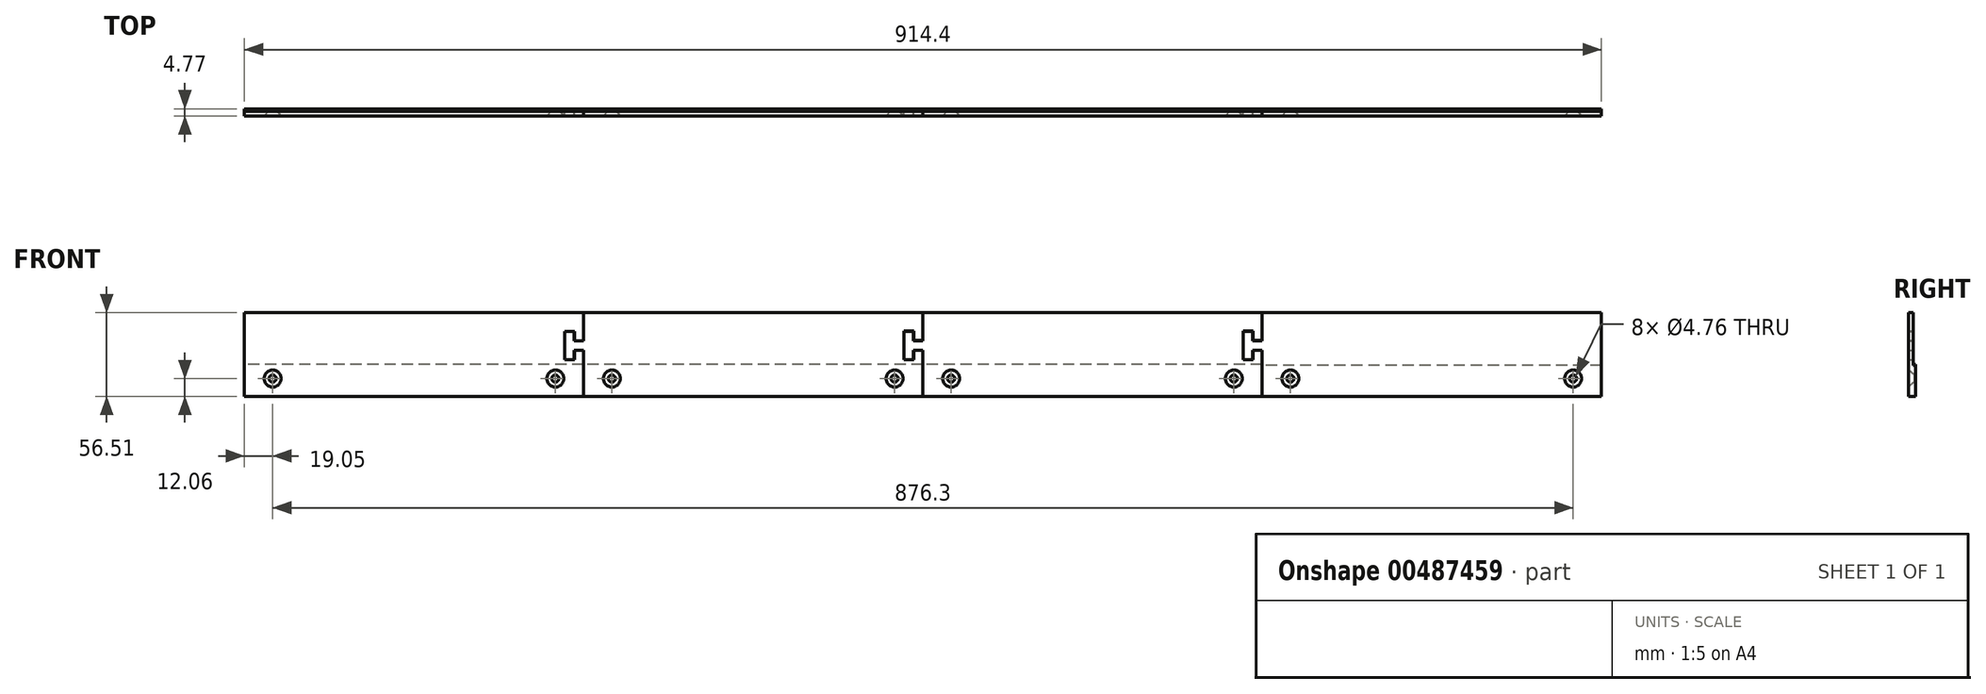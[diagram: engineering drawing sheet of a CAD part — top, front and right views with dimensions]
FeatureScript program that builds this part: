
annotation { "Feature Type Name" : "Feature", "Feature Type Description" : "" }
export const myFeature = defineFeature(function(context is Context, id is Id, definition is map)
    precondition{}
    {
        {
            var Q0;
            Q0=qCreatedBy(makeId("Front.planeOp"),FACE);
            var sketch = newSketch(context, id + "F0", { "sketchPlane" : qUnion([Q0])});
            skLineSegment(sketch, "E0.bottom", {"start": v(0, 0) * mm, "end": v(228.45, 0) * mm});
            skLineSegment(sketch, "E0.top", {"start": v(0, -63.5) * mm, "end": v(228.45, -63.5) * mm});
            skLineSegment(sketch, "E0.right", {"start": v(457.2, 0) * mm, "end": v(457.2, -63.5) * mm});
            skCircle(sketch, "E1", {"center": v(438.15, -44.45) * mm, "radius": 2.38 * mm});
            skLineSegment(sketch, "E2.MirrorCS", {"start": v(-0.15, 0) * mm, "end": v(-228.6, 0) * mm});
            skLineSegment(sketch, "E3.MirrorCS", {"start": v(-0.15, -63.5) * mm, "end": v(-228.6, -63.5) * mm});
            skLineSegment(sketch, "E4.MirrorCS", {"start": v(-457.2, 0) * mm, "end": v(-457.2, -63.5) * mm});
            skCircle(sketch, "E5.MirrorC", {"center": v(-438.15, -44.45) * mm, "radius": 2.38 * mm});
            skLineSegment(sketch, "E6", {"start": v(-228.6, 0) * mm, "end": v(-228.6, -19.05) * mm});
            skLineSegment(sketch, "E7", {"start": v(0, 0) * mm, "end": v(0, -18.9) * mm});
            skLineSegment(sketch, "E8", {"start": v(228.6, 0) * mm, "end": v(228.6, -18.9) * mm});
            skLineSegment(sketch, "E9", {"start": v(-228.6, -19.05) * mm, "end": v(-234.95, -19.05) * mm});
            skLineSegment(sketch, "E10", {"start": v(-234.95, -19.05) * mm, "end": v(-234.95, -12.7) * mm});
            skLineSegment(sketch, "E11", {"start": v(-234.95, -12.7) * mm, "end": v(-241.3, -12.7) * mm});
            skLineSegment(sketch, "E12", {"start": v(-241.3, -12.7) * mm, "end": v(-241.3, -31.75) * mm});
            skLineSegment(sketch, "E13", {"start": v(-241.3, -31.75) * mm, "end": v(-234.95, -31.75) * mm});
            skLineSegment(sketch, "E14", {"start": v(-234.95, -31.75) * mm, "end": v(-234.95, -25.4) * mm});
            skLineSegment(sketch, "E15", {"start": v(-234.95, -25.4) * mm, "end": v(-228.6, -25.4) * mm});
            skLineSegment(sketch, "E16", {"start": v(-228.75, 0) * mm, "end": v(-228.75, -18.9) * mm});
            skLineSegment(sketch, "E17", {"start": v(-228.75, -18.9) * mm, "end": v(-234.8, -18.9) * mm});
            skLineSegment(sketch, "E18", {"start": v(-234.8, -18.9) * mm, "end": v(-234.8, -12.55) * mm});
            skLineSegment(sketch, "E19", {"start": v(-234.8, -12.55) * mm, "end": v(-241.45, -12.55) * mm});
            skLineSegment(sketch, "E20", {"start": v(-241.45, -12.55) * mm, "end": v(-241.45, -31.9) * mm});
            skLineSegment(sketch, "E21.MirrorCS", {"start": v(-228.75, -63.5) * mm, "end": v(-228.75, -25.55) * mm});
            skLineSegment(sketch, "E22.MirrorCS", {"start": v(-228.75, -25.55) * mm, "end": v(-234.8, -25.55) * mm});
            skLineSegment(sketch, "E23.MirrorCS", {"start": v(-234.8, -25.55) * mm, "end": v(-234.8, -31.9) * mm});
            skLineSegment(sketch, "E24.MirrorCS", {"start": v(-234.8, -31.9) * mm, "end": v(-241.45, -31.9) * mm});
            skLineSegment(sketch, "E25.trimOffspring", {"start": v(-228.75, 0) * mm, "end": v(-457.2, 0) * mm});
            skLineSegment(sketch, "E26.trimOffspring", {"start": v(-228.6, -25.4) * mm, "end": v(-228.6, -63.5) * mm});
            skCircle(sketch, "E27", {"center": v(-247.65, -44.45) * mm, "radius": 2.38 * mm});
            skCircle(sketch, "E28.MirrorC", {"center": v(-209.55, -44.45) * mm, "radius": 2.38 * mm});
            skCircle(sketch, "E29.MirrorC", {"center": v(-19.05, -44.45) * mm, "radius": 2.38 * mm});
            skLineSegment(sketch, "E30.trimOffspring", {"start": v(-228.75, -63.5) * mm, "end": v(-457.2, -63.5) * mm});
            skCircle(sketch, "E31.MirrorC", {"center": v(19.05, -44.45) * mm, "radius": 2.38 * mm});
            skCircle(sketch, "E32.MirrorC", {"center": v(209.55, -44.45) * mm, "radius": 2.38 * mm});
            skCircle(sketch, "E33.MirrorC", {"center": v(247.65, -44.45) * mm, "radius": 2.38 * mm});
            skLineSegment(sketch, "E34", {"start": v(0, -18.9) * mm, "end": v(-6.35, -18.9) * mm});
            skLineSegment(sketch, "E35", {"start": v(-6.35, -18.9) * mm, "end": v(-6.35, -12.55) * mm});
            skLineSegment(sketch, "E36", {"start": v(-6.35, -12.55) * mm, "end": v(-12.7, -12.55) * mm});
            skLineSegment(sketch, "E37", {"start": v(-12.7, -12.55) * mm, "end": v(-12.7, -31.6) * mm});
            skLineSegment(sketch, "E38", {"start": v(-12.7, -31.6) * mm, "end": v(-6.35, -31.6) * mm});
            skLineSegment(sketch, "E39", {"start": v(-6.35, -31.6) * mm, "end": v(-6.35, -25.25) * mm});
            skLineSegment(sketch, "E40", {"start": v(-6.35, -25.25) * mm, "end": v(0, -25.25) * mm});
            skLineSegment(sketch, "E41", {"start": v(-0.15, -18.75) * mm, "end": v(-6.2, -18.75) * mm});
            skLineSegment(sketch, "E42", {"start": v(-6.2, -18.75) * mm, "end": v(-6.2, -12.4) * mm});
            skLineSegment(sketch, "E43", {"start": v(-6.2, -12.4) * mm, "end": v(-12.85, -12.4) * mm});
            skLineSegment(sketch, "E44", {"start": v(-12.85, -12.4) * mm, "end": v(-12.85, -31.75) * mm});
            skLineSegment(sketch, "E45.MirrorCS", {"start": v(-0.15, -25.4) * mm, "end": v(-6.2, -25.4) * mm});
            skLineSegment(sketch, "E46.MirrorCS", {"start": v(-6.2, -25.4) * mm, "end": v(-6.2, -31.75) * mm});
            skLineSegment(sketch, "E47.MirrorCS", {"start": v(-6.2, -31.75) * mm, "end": v(-12.85, -31.75) * mm});
            skLineSegment(sketch, "E48", {"start": v(-0.15, -18.75) * mm, "end": v(-0.15, 0) * mm});
            skLineSegment(sketch, "E49", {"start": v(-0.15, -25.4) * mm, "end": v(-0.15, -63.5) * mm});
            skLineSegment(sketch, "E50.trimOffspring", {"start": v(0, -25.25) * mm, "end": v(0, -63.5) * mm});
            skLineSegment(sketch, "E51", {"start": v(228.6, -18.9) * mm, "end": v(222.25, -18.9) * mm});
            skLineSegment(sketch, "E52", {"start": v(222.25, -18.9) * mm, "end": v(222.25, -12.55) * mm});
            skLineSegment(sketch, "E53", {"start": v(222.25, -12.55) * mm, "end": v(215.9, -12.55) * mm});
            skLineSegment(sketch, "E54", {"start": v(215.9, -12.55) * mm, "end": v(215.9, -31.6) * mm});
            skLineSegment(sketch, "E55", {"start": v(215.9, -31.6) * mm, "end": v(222.25, -31.6) * mm});
            skLineSegment(sketch, "E56", {"start": v(222.25, -31.6) * mm, "end": v(222.25, -25.25) * mm});
            skLineSegment(sketch, "E57", {"start": v(222.25, -25.25) * mm, "end": v(228.6, -25.25) * mm});
            skLineSegment(sketch, "E58", {"start": v(228.45, -18.75) * mm, "end": v(222.4, -18.75) * mm});
            skLineSegment(sketch, "E59", {"start": v(222.4, -18.75) * mm, "end": v(222.4, -12.4) * mm});
            skLineSegment(sketch, "E60", {"start": v(222.4, -12.4) * mm, "end": v(215.75, -12.4) * mm});
            skLineSegment(sketch, "E61", {"start": v(215.75, -12.4) * mm, "end": v(215.75, -31.75) * mm});
            skLineSegment(sketch, "E62.MirrorCS", {"start": v(228.45, -25.4) * mm, "end": v(222.4, -25.4) * mm});
            skLineSegment(sketch, "E63.MirrorCS", {"start": v(222.4, -25.4) * mm, "end": v(222.4, -31.75) * mm});
            skLineSegment(sketch, "E64.MirrorCS", {"start": v(222.4, -31.75) * mm, "end": v(215.75, -31.75) * mm});
            skLineSegment(sketch, "E65", {"start": v(228.45, -18.75) * mm, "end": v(228.45, 0) * mm});
            skLineSegment(sketch, "E66", {"start": v(228.45, -25.4) * mm, "end": v(228.45, -63.5) * mm});
            skLineSegment(sketch, "E67.trimOffspring", {"start": v(228.6, -63.5) * mm, "end": v(457.2, -63.5) * mm});
            skLineSegment(sketch, "E68.trimOffspring", {"start": v(228.6, 0) * mm, "end": v(457.2, 0) * mm});
            skLineSegment(sketch, "E69.trimOffspring", {"start": v(228.6, -25.25) * mm, "end": v(228.6, -63.5) * mm});
            skSolve(sketch);
        }
        {
            var Q0;
            Q0 = qSketchRegion(id + "F0", true);
            extrude(context, id + "F1", {"entities" : qUnion([Q0]), "depth" : 3.17 * mm, "offsetDistance" : 25.4 * mm});
        }
        {
            var Q0;
            Q0=makeQuery(id+"F1.opExtrude","CAP_FACE",FACE,{"disambiguationData":[OSD([sQuery(id+"F0.wireOp",EDGE,"E0.right"),sQuery(id+"F0.wireOp",EDGE,"E1"),sQuery(id+"F0.wireOp",EDGE,"E8"),sQuery(id+"F0.wireOp",EDGE,"E33.MirrorC"),sQuery(id+"F0.wireOp",EDGE,"E51"),sQuery(id+"F0.wireOp",EDGE,"E52"),sQuery(id+"F0.wireOp",EDGE,"E53"),sQuery(id+"F0.wireOp",EDGE,"E54"),sQuery(id+"F0.wireOp",EDGE,"E55"),sQuery(id+"F0.wireOp",EDGE,"E56"),sQuery(id+"F0.wireOp",EDGE,"E57"),sQuery(id+"F0.wireOp",EDGE,"E67.trimOffspring"),sQuery(id+"F0.wireOp",EDGE,"E68.trimOffspring"),sQuery(id+"F0.wireOp",EDGE,"E69.trimOffspring")])],"isStart":true});
            var sketch = newSketch(context, id + "F2", { "sketchPlane" : qUnion([Q0])});
            skLineSegment(sketch, "E70.bottom", {"start": v(-457.2, -35.72) * mm, "end": v(-228.6, -35.72) * mm});
            skLineSegment(sketch, "E70.top", {"start": v(-457.2, -63.5) * mm, "end": v(-228.6, -63.5) * mm});
            skLineSegment(sketch, "E70.left", {"start": v(-457.2, -35.72) * mm, "end": v(-457.2, -63.5) * mm});
            skLineSegment(sketch, "E70.right", {"start": v(-228.6, -35.72) * mm, "end": v(-228.6, -63.5) * mm});
            skLineSegment(sketch, "E71.bottom", {"start": v(-228.45, -34.93) * mm, "end": v(0, -34.93) * mm});
            skLineSegment(sketch, "E71.top", {"start": v(-228.45, -63.5) * mm, "end": v(0, -63.5) * mm});
            skLineSegment(sketch, "E71.left", {"start": v(-228.45, -34.93) * mm, "end": v(-228.45, -63.5) * mm});
            skLineSegment(sketch, "E71.right", {"start": v(0, -34.93) * mm, "end": v(0, -63.5) * mm});
            skLineSegment(sketch, "E72.bottom", {"start": v(0.15, -34.93) * mm, "end": v(228.6, -34.93) * mm});
            skLineSegment(sketch, "E72.top", {"start": v(0.15, -63.5) * mm, "end": v(228.6, -63.5) * mm});
            skLineSegment(sketch, "E72.left", {"start": v(0.15, -34.93) * mm, "end": v(0.15, -63.5) * mm});
            skLineSegment(sketch, "E72.right", {"start": v(228.6, -34.93) * mm, "end": v(228.6, -63.5) * mm});
            skLineSegment(sketch, "E73.bottom", {"start": v(228.75, -34.93) * mm, "end": v(457.2, -34.93) * mm});
            skLineSegment(sketch, "E73.top", {"start": v(228.75, -63.5) * mm, "end": v(457.2, -63.5) * mm});
            skLineSegment(sketch, "E73.left", {"start": v(228.75, -34.93) * mm, "end": v(228.75, -63.5) * mm});
            skLineSegment(sketch, "E73.right", {"start": v(457.2, -34.93) * mm, "end": v(457.2, -63.5) * mm});
            skCircle(sketch, "E74", {"center": v(-438.15, -44.45) * mm, "radius": 2.38 * mm});
            skCircle(sketch, "E75", {"center": v(-247.65, -44.45) * mm, "radius": 2.38 * mm});
            skCircle(sketch, "E76.MirrorC", {"center": v(-209.55, -44.45) * mm, "radius": 2.38 * mm});
            skCircle(sketch, "E77.MirrorC", {"center": v(-19.05, -44.45) * mm, "radius": 2.38 * mm});
            skCircle(sketch, "E78.MirrorC", {"center": v(19.05, -44.45) * mm, "radius": 2.38 * mm});
            skCircle(sketch, "E79.MirrorC", {"center": v(209.55, -44.45) * mm, "radius": 2.38 * mm});
            skCircle(sketch, "E80.MirrorC", {"center": v(247.65, -44.45) * mm, "radius": 2.38 * mm});
            skCircle(sketch, "E81.MirrorC", {"center": v(438.15, -44.45) * mm, "radius": 2.38 * mm});
            skSolve(sketch);
        }
        {
            var Q0;
            Q0 = qSketchRegion(id + "F2", true);
            extrude(context, id + "F3", {"entities" : qUnion([Q0]), "operationType" : NewBodyOperationType.ADD, "depth" : 1.59 * mm, "offsetDistance" : 25.4 * mm, "hasSecondDirection" : true, "secondDirectionOppositeDirection" : true, "secondDirectionDepth" : 1.27 * mm});
        }
        {
            var Q0;
            Q0=makeQuery(id+"F1.opExtrude","CAP_EDGE",EDGE,{"disambiguationData":[OSD([sQuery(id+"F0.wireOp",EDGE,"E1")])],"isStart":false});
            var Q1;
            Q1=makeQuery(id+"F1.opExtrude","CAP_EDGE",EDGE,{"disambiguationData":[OSD([sQuery(id+"F0.wireOp",EDGE,"E33.MirrorC")])],"isStart":false});
            var Q2;
            Q2=makeQuery(id+"F1.opExtrude","CAP_EDGE",EDGE,{"disambiguationData":[OSD([sQuery(id+"F0.wireOp",EDGE,"E32.MirrorC")])],"isStart":false});
            var Q3;
            Q3=makeQuery(id+"F1.opExtrude","CAP_EDGE",EDGE,{"disambiguationData":[OSD([sQuery(id+"F0.wireOp",EDGE,"E31.MirrorC")])],"isStart":false});
            var Q4;
            Q4=makeQuery(id+"F1.opExtrude","CAP_EDGE",EDGE,{"disambiguationData":[OSD([sQuery(id+"F0.wireOp",EDGE,"E29.MirrorC")])],"isStart":false});
            var Q5;
            Q5=makeQuery(id+"F1.opExtrude","CAP_EDGE",EDGE,{"disambiguationData":[OSD([sQuery(id+"F0.wireOp",EDGE,"E28.MirrorC")])],"isStart":false});
            var Q6;
            Q6=makeQuery(id+"F1.opExtrude","CAP_EDGE",EDGE,{"disambiguationData":[OSD([sQuery(id+"F0.wireOp",EDGE,"E27")])],"isStart":false});
            var Q7;
            Q7=makeQuery(id+"F1.opExtrude","CAP_EDGE",EDGE,{"disambiguationData":[OSD([sQuery(id+"F0.wireOp",EDGE,"E5.MirrorC")])],"isStart":false});
            chamfer(context, id + "F4", {"entities" : qUnion([Q0, Q1, Q2, Q3, Q4, Q5, Q6, Q7]), "chamferType" : ChamferType.OFFSET_ANGLE, "width" : 3.8 * mm, "oppositeDirection" : false, "angle" : 41 * degree, "tangentPropagation" : true});
        }
        {
            var Q0;
            Q0=makeQuery(id+"F1.opExtrude","CAP_FACE",FACE,{"disambiguationData":[OSD([sQuery(id+"F0.wireOp",EDGE,"E4.MirrorCS"),sQuery(id+"F0.wireOp",EDGE,"E5.MirrorC"),sQuery(id+"F0.wireOp",EDGE,"E16"),sQuery(id+"F0.wireOp",EDGE,"E17"),sQuery(id+"F0.wireOp",EDGE,"E18"),sQuery(id+"F0.wireOp",EDGE,"E19"),sQuery(id+"F0.wireOp",EDGE,"E20"),sQuery(id+"F0.wireOp",EDGE,"E21.MirrorCS"),sQuery(id+"F0.wireOp",EDGE,"E22.MirrorCS"),sQuery(id+"F0.wireOp",EDGE,"E23.MirrorCS"),sQuery(id+"F0.wireOp",EDGE,"E24.MirrorCS"),sQuery(id+"F0.wireOp",EDGE,"E25.trimOffspring"),sQuery(id+"F0.wireOp",EDGE,"E27"),sQuery(id+"F0.wireOp",EDGE,"E30.trimOffspring")])],"isStart":false});
            var sketch = newSketch(context, id + "F5", { "sketchPlane" : qUnion([Q0])});
            skLineSegment(sketch, "E82.bottom", {"start": v(-469.14, -56.51) * mm, "end": v(546.86, -56.51) * mm});
            skLineSegment(sketch, "E82.top", {"start": v(-469.14, -107.31) * mm, "end": v(546.86, -107.31) * mm});
            skLineSegment(sketch, "E82.left", {"start": v(-469.14, -56.51) * mm, "end": v(-469.14, -107.31) * mm});
            skLineSegment(sketch, "E82.right", {"start": v(546.86, -56.51) * mm, "end": v(546.86, -107.31) * mm});
            skSolve(sketch);
        }
        {
            var Q0;
            Q0 = qSketchRegion(id + "F5", true);
            var Q1;
            Q1 = qConstructionFilter(qBodyType(qCreatedBy(id + "F5" ,EDGE), BodyType.WIRE), ConstructionObject.NO);
            extrude(context, id + "F6", {"entities" : qUnion([Q0]), "operationType" : NewBodyOperationType.REMOVE, "surfaceEntities" : qUnion([Q1]), "oppositeDirection" : true, "depth" : 109.98 * mm, "offsetDistance" : 25.4 * mm});
        }
    });
